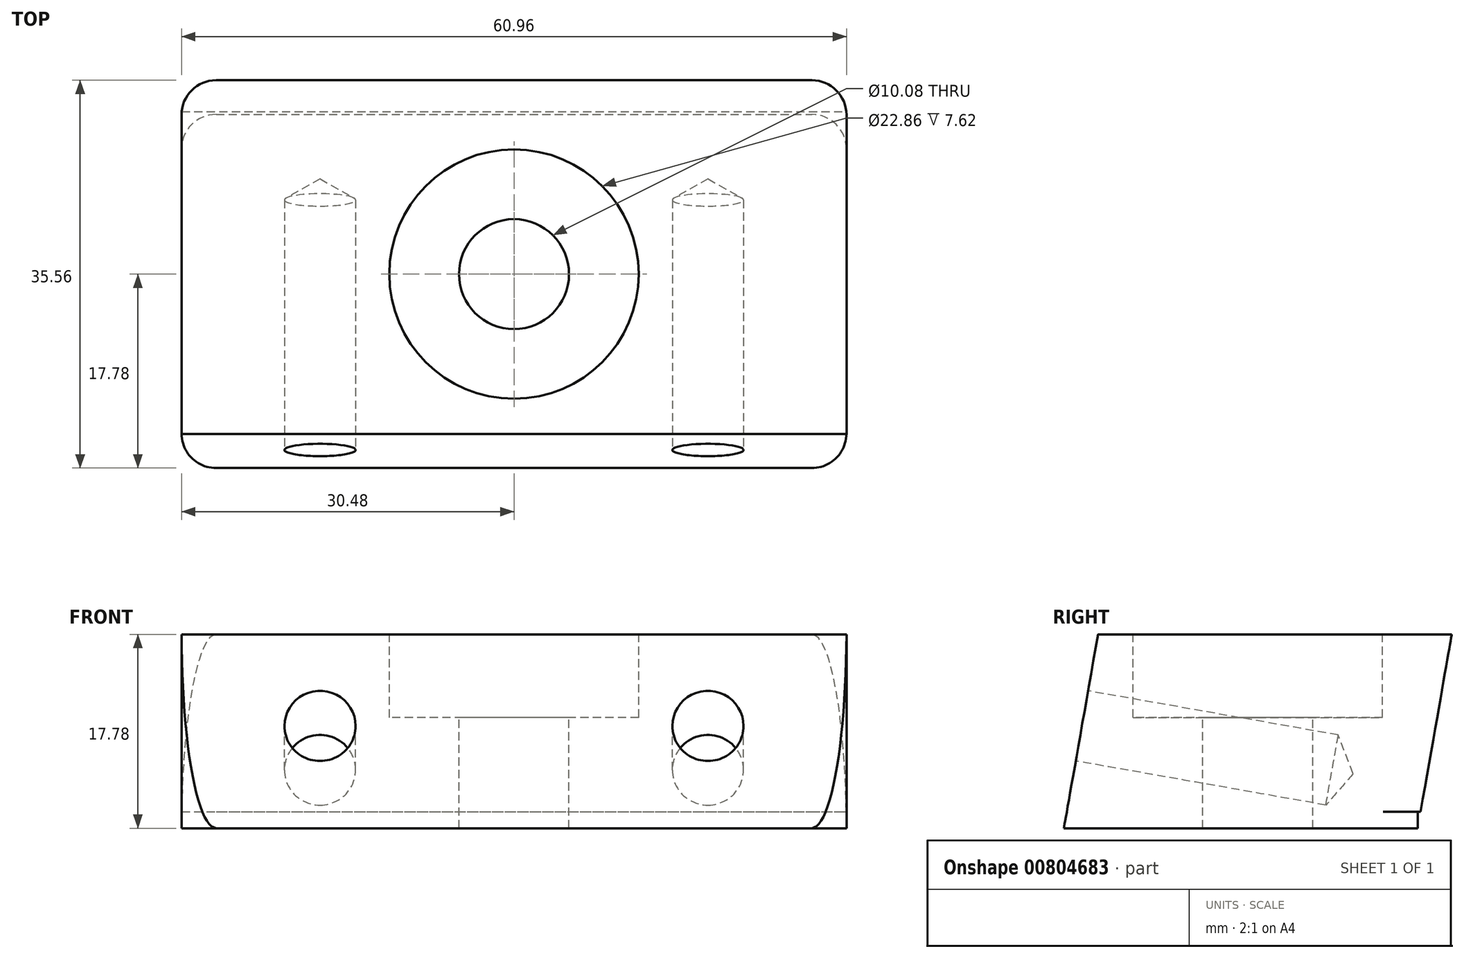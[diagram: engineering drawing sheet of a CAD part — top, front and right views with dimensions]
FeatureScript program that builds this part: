
annotation { "Feature Type Name" : "Feature", "Feature Type Description" : "" }
export const myFeature = defineFeature(function(context is Context, id is Id, definition is map)
    precondition{}
    {
        {
            var Q0;
            Q0=qCreatedBy(makeId("Top.planeOp"),FACE);
            var sketch = newSketch(context, id + "F0", { "sketchPlane" : qUnion([Q0])});
            skLineSegment(sketch, "E0.bottom", {"start": v(0, 0) * mm, "end": v(60.96, 0) * mm});
            skLineSegment(sketch, "E0.top", {"start": v(0, 35.56) * mm, "end": v(60.96, 35.56) * mm});
            skLineSegment(sketch, "E0.left", {"start": v(0, 0) * mm, "end": v(0, 35.56) * mm});
            skLineSegment(sketch, "E0.right", {"start": v(60.96, 0) * mm, "end": v(60.96, 35.56) * mm});
            skSolve(sketch);
        }
        {
            var Q0;
            Q0=makeQuery(id+"F0.imprint","IMPRINT",FACE,{"disambiguationData":[TD([[makeQuery(id+"F0.imprint","IMPRINT",EDGE,{"derivedFrom":sQuery(id+"F0.wireOp",EDGE,"E0.bottom")}),1.0]])]});
            extrude(context, id + "F1", {"entities" : qUnion([Q0]), "depth" : 17.78 * mm, "offsetDistance" : 25.4 * mm});
        }
        {
            var Q0;
            Q0=makeQuery(id+"F1.opExtrude","SWEPT_EDGE",EDGE,{"disambiguationData":[OSD([sQuery(id+"F0.wireOp",EDGE,"E0.bottom"),sQuery(id+"F0.wireOp",EDGE,"E0.left")])]});
            var Q1;
            Q1=makeQuery(id+"F1.opExtrude","SWEPT_EDGE",EDGE,{"disambiguationData":[OSD([sQuery(id+"F0.wireOp",EDGE,"E0.bottom"),sQuery(id+"F0.wireOp",EDGE,"E0.right")])]});
            var Q2;
            Q2=makeQuery(id+"F1.opExtrude","SWEPT_EDGE",EDGE,{"disambiguationData":[OSD([sQuery(id+"F0.wireOp",EDGE,"E0.top"),sQuery(id+"F0.wireOp",EDGE,"E0.right")])]});
            var Q3;
            Q3=makeQuery(id+"F1.opExtrude","SWEPT_EDGE",EDGE,{"disambiguationData":[OSD([sQuery(id+"F0.wireOp",EDGE,"E0.top"),sQuery(id+"F0.wireOp",EDGE,"E0.left")])]});
            fillet(context, id + "F2", {"entities" : qUnion([Q0, Q1, Q2, Q3]), "radius" : 3.17 * mm, "tangentPropagation" : true, "allowEdgeOverflow" : false});
        }
        {
            var Q0;
            Q0=makeQuery(id+"F1.opExtrude","SWEPT_FACE",FACE,{"disambiguationData":[OSD([sQuery(id+"F0.wireOp",EDGE,"E0.right")])]});
            var sketch = newSketch(context, id + "F3", { "sketchPlane" : qUnion([Q0])});
            skLineSegment(sketch, "E1", {"start": v(0, 0) * mm, "end": v(3.14, 17.78) * mm});
            skPoint(sketch, "E2.0", {"position": v(35.56, 17.78) * mm});
            skLineSegment(sketch, "E3.0.0", {"start": v(35.56, 17.78) * mm, "end": v(32.38, 17.78) * mm});
            skLineSegment(sketch, "E3.0.1", {"start": v(32.38, 0) * mm, "end": v(32.38, 17.78) * mm});
            skLineSegment(sketch, "E3.0.2", {"start": v(35.56, 0) * mm, "end": v(32.38, 0) * mm});
            skLineSegment(sketch, "E3.0.3", {"start": v(35.56, 0) * mm, "end": v(35.56, 17.78) * mm});
            skLineSegment(sketch, "E4.0.0", {"start": v(32.38, 17.78) * mm, "end": v(3.17, 17.78) * mm});
            skLineSegment(sketch, "E4.0.1", {"start": v(3.17, 17.78) * mm, "end": v(3.17, 0) * mm});
            skLineSegment(sketch, "E4.0.2", {"start": v(3.17, 0) * mm, "end": v(32.38, 0) * mm});
            skLineSegment(sketch, "E5.0.0", {"start": v(3.17, 17.78) * mm, "end": v(0, 17.78) * mm});
            skLineSegment(sketch, "E5.0.1", {"start": v(0, 0) * mm, "end": v(0, 17.78) * mm});
            skLineSegment(sketch, "E5.0.2", {"start": v(3.17, 0) * mm, "end": v(0, 0) * mm});
            skLineSegment(sketch, "E5.0.3", {"start": v(3.17, 0) * mm, "end": v(3.17, 17.78) * mm});
            skLineSegment(sketch, "E6", {"start": v(35.56, 17.78) * mm, "end": v(32.7, 1.52) * mm});
            skLineSegment(sketch, "E7", {"start": v(32.42, 0) * mm, "end": v(32.42, 1.52) * mm});
            skLineSegment(sketch, "E8", {"start": v(32.42, 1.52) * mm, "end": v(32.7, 1.52) * mm});
            skLineSegment(sketch, "E9", {"start": v(32.42, 0) * mm, "end": v(35.56, 0) * mm});
            skSolve(sketch);
        }
        {
            var Q0;
            {var subQ1=sQuery(id+"F3.wireOp",EDGE,"E7");Q0=makeQuery(id+"F3.imprint","IMPRINT",FACE,{"disambiguationData":[TD([[makeQuery(id+"F3.imprint","IMPRINT",EDGE,{"derivedFrom":subQ1}),-1.0]])]});}
            var Q1;
            {var subQ5=sQuery(id+"F3.wireOp",EDGE,"E3.0.3");Q1=makeQuery(id+"F3.imprint","IMPRINT",FACE,{"disambiguationData":[TD([[makeQuery(id+"F3.imprint","IMPRINT",EDGE,{"derivedFrom":subQ5}),1.0]])]});}
            var Q2;
            {var subQ4=sQuery(id+"F3.wireOp",EDGE,"E5.0.0");Q2=makeQuery(id+"F3.imprint","IMPRINT",FACE,{"disambiguationData":[TD([[makeQuery(id+"F3.imprint","IMPRINT",EDGE,{"derivedFrom":subQ4}),1.0]])]});}
            var Q3;
            {var subQ0=sQuery(id+"F3.wireOp",EDGE,"E4.0.0");var subQ1=sQuery(id+"F3.wireOp",EDGE,"E1");var subQ2=makeQuery(id+"F3.imprint","INTERSECT",VERTEX,{"derivedFrom":[subQ1,subQ0]});Q3=makeQuery(id+"F3.imprint","IMPRINT",FACE,{"disambiguationData":[TD([[makeQuery(id+"F3.imprint","IMPRINT",EDGE,{"disambiguationData":[TD([[subQ2,1.0]])],"derivedFrom":subQ1}),1.0]])]});}
            extrude(context, id + "F4", {"entities" : qUnion([Q0, Q1, Q2, Q3]), "operationType" : NewBodyOperationType.REMOVE, "endBound" : BoundingType.THROUGH_ALL, "oppositeDirection" : true, "depth" : 25.4 * mm, "offsetDistance" : 25.4 * mm});
        }
        {
            var Q0;
            Q0=makeQuery(id+"F1.opExtrude","CAP_FACE",FACE,{"disambiguationData":[OSD([sQuery(id+"F0.wireOp",EDGE,"E0.bottom"),sQuery(id+"F0.wireOp",EDGE,"E0.top"),sQuery(id+"F0.wireOp",EDGE,"E0.left"),sQuery(id+"F0.wireOp",EDGE,"E0.right")])],"isStart":false});
            var sketch = newSketch(context, id + "F5", { "sketchPlane" : qUnion([Q0])});
            skArc(sketch, "E10.0.0", {"start": v(0, 32.39) * mm, "mid": v(0, 32.4) * mm, "end": v(0, 32.42) * mm});
            skLineSegment(sketch, "E10.0.1", {"start": v(0, 32.42) * mm, "end": v(60.96, 32.42) * mm});
            skArc(sketch, "E10.0.2", {"start": v(60.96, 32.42) * mm, "mid": v(60.96, 32.4) * mm, "end": v(60.96, 32.39) * mm});
            skLineSegment(sketch, "E10.0.3", {"start": v(60.96, 32.39) * mm, "end": v(60.96, 3.18) * mm});
            skArc(sketch, "E10.0.4", {"start": v(60.96, 3.18) * mm, "mid": v(60.03, 0.93) * mm, "end": v(57.79, 0) * mm});
            skLineSegment(sketch, "E10.0.5", {"start": v(57.79, 0) * mm, "end": v(3.18, 0) * mm});
            skArc(sketch, "E10.0.6", {"start": v(3.18, 0) * mm, "mid": v(0.93, 0.93) * mm, "end": v(0, 3.17) * mm});
            skLineSegment(sketch, "E10.0.7", {"start": v(0, 3.18) * mm, "end": v(0, 32.39) * mm});
            skArc(sketch, "E11.0.0", {"start": v(0, 3.17) * mm, "mid": v(0, 3.16) * mm, "end": v(0, 3.14) * mm});
            skLineSegment(sketch, "E11.0.1", {"start": v(0, 3.14) * mm, "end": v(60.96, 3.14) * mm});
            skArc(sketch, "E11.0.2", {"start": v(60.96, 3.14) * mm, "mid": v(60.96, 3.16) * mm, "end": v(60.96, 3.18) * mm});
            skLineSegment(sketch, "E11.0.3", {"start": v(60.96, 3.18) * mm, "end": v(60.96, 32.39) * mm});
            skArc(sketch, "E11.0.4", {"start": v(60.96, 32.39) * mm, "mid": v(60.03, 34.63) * mm, "end": v(57.78, 35.56) * mm});
            skLineSegment(sketch, "E11.0.5", {"start": v(57.78, 35.56) * mm, "end": v(3.17, 35.56) * mm});
            skArc(sketch, "E11.0.6", {"start": v(3.17, 35.56) * mm, "mid": v(0.93, 34.63) * mm, "end": v(0, 32.39) * mm});
            skLineSegment(sketch, "E11.0.7", {"start": v(0, 32.39) * mm, "end": v(0, 3.18) * mm});
            skLineSegment(sketch, "E12", {"start": v(0, 3.14) * mm, "end": v(0, 32.42) * mm});
            skLineSegment(sketch, "E13", {"start": v(0, 17.78) * mm, "end": v(60.96, 17.78) * mm, "construction": true});
            skPoint(sketch, "E14", {"position": v(30.48, 17.78) * mm});
            skSolve(sketch);
        }
        {
            var Q0;
            Q0=sQuery(id+"F5.wireOp",VERTEX,"E14");
            var Q1;
            Q1=makeQuery(id+"F1.opExtrude","SWEPT_BODY",BODY,{"disambiguationData":[OSD([sQuery(id+"F0.wireOp",EDGE,"E0.bottom"),sQuery(id+"F0.wireOp",EDGE,"E0.top"),sQuery(id+"F0.wireOp",EDGE,"E0.left"),sQuery(id+"F0.wireOp",EDGE,"E0.right")])]});
            hole(context, id + "F6", {"style" : HoleStyle.C_BORE, "endStyle" : HoleEndStyle.BLIND, "holeDiameter" : 10.08 * mm, "cBoreDiameter" : 22.86 * mm, "cBoreDepth" : 7.62 * mm, "majorDiameter" : 6.35 * mm, "holeDepth" : 23.3 * mm, "isTappedThrough" : true, "tappedDepth" : 19.05 * mm, "tapClearance" : 3, "locations" : qUnion([Q0]), "scope" : qUnion([Q1])});
        }
        {
            var Q0;
            Q0=makeQuery(id+"F4.boolean.opBoolean","INTERSECT",EDGE,{"derivedFrom":[makeQuery(id+"F2.opFillet","BLEND_FACE",FACE,{"disambiguationData":[OSD([sQuery(id+"F0.wireOp",EDGE,"E0.top"),sQuery(id+"F0.wireOp",EDGE,"E0.right")])]}),makeQuery(id+"F4.opExtrude","SWEPT_FACE",FACE,{"disambiguationData":[OSD([sQuery(id+"F3.wireOp",EDGE,"E7")])]})]});
            var Q1;
            Q1=makeQuery(id+"F4.boolean.opBoolean","INTERSECT",EDGE,{"derivedFrom":[makeQuery(id+"F2.opFillet","BLEND_FACE",FACE,{"disambiguationData":[OSD([sQuery(id+"F0.wireOp",EDGE,"E0.top"),sQuery(id+"F0.wireOp",EDGE,"E0.left")])]}),makeQuery(id+"F4.opExtrude","SWEPT_FACE",FACE,{"disambiguationData":[OSD([sQuery(id+"F3.wireOp",EDGE,"E7")])]})]});
            fillet(context, id + "F7", {"entities" : qUnion([Q0, Q1]), "radius" : 3.17 * mm, "tangentPropagation" : true, "allowEdgeOverflow" : false});
        }
        {
            var Q0;
            Q0=makeQuery(id+"F4.boolean.opBoolean","COPY",FACE,{"derivedFrom":makeQuery(id+"F4.opExtrude","SWEPT_FACE",FACE,{"disambiguationData":[OSD([sQuery(id+"F3.wireOp",EDGE,"E1")])]})});
            var sketch = newSketch(context, id + "F8", { "sketchPlane" : qUnion([Q0])});
            skPoint(sketch, "E15", {"position": v(12.7, 9.52) * mm});
            skPoint(sketch, "E16", {"position": v(48.26, 9.53) * mm});
            skSolve(sketch);
        }
        {
            var Q0;
            Q0=sQuery(id+"F8.wireOp",VERTEX,"E15");
            var Q1;
            Q1=sQuery(id+"F8.wireOp",VERTEX,"E16");
            var Q2;
            Q2=makeQuery(id+"F1.opExtrude","SWEPT_BODY",BODY,{"disambiguationData":[OSD([sQuery(id+"F0.wireOp",EDGE,"E0.bottom"),sQuery(id+"F0.wireOp",EDGE,"E0.top"),sQuery(id+"F0.wireOp",EDGE,"E0.left"),sQuery(id+"F0.wireOp",EDGE,"E0.right")])]});
            hole(context, id + "F9", {"style" : HoleStyle.SIMPLE, "endStyle" : HoleEndStyle.BLIND, "standardTappedOrClearance" : lookupTablePath({ "standard" : "ANSI", "engagement" : "75%", "pitch" : "18 tpi", "size" : "5/16", "type" : "Tapped" }), "standardBlindInLast" : lookupTablePath({ "standard" : "ANSI", "engagement" : "75%", "pitch" : "18 tpi", "size" : "5/16", "type" : "Tapped" }), "holeDiameter" : 6.53 * mm, "majorDiameter" : 7.94 * mm, "showTappedDepth" : true, "holeDepth" : 23.28 * mm, "isTappedThrough" : true, "tappedDepth" : 19.05 * mm, "tapClearance" : 3, "locations" : qUnion([Q0, Q1]), "scope" : qUnion([Q2])});
        }
    });
